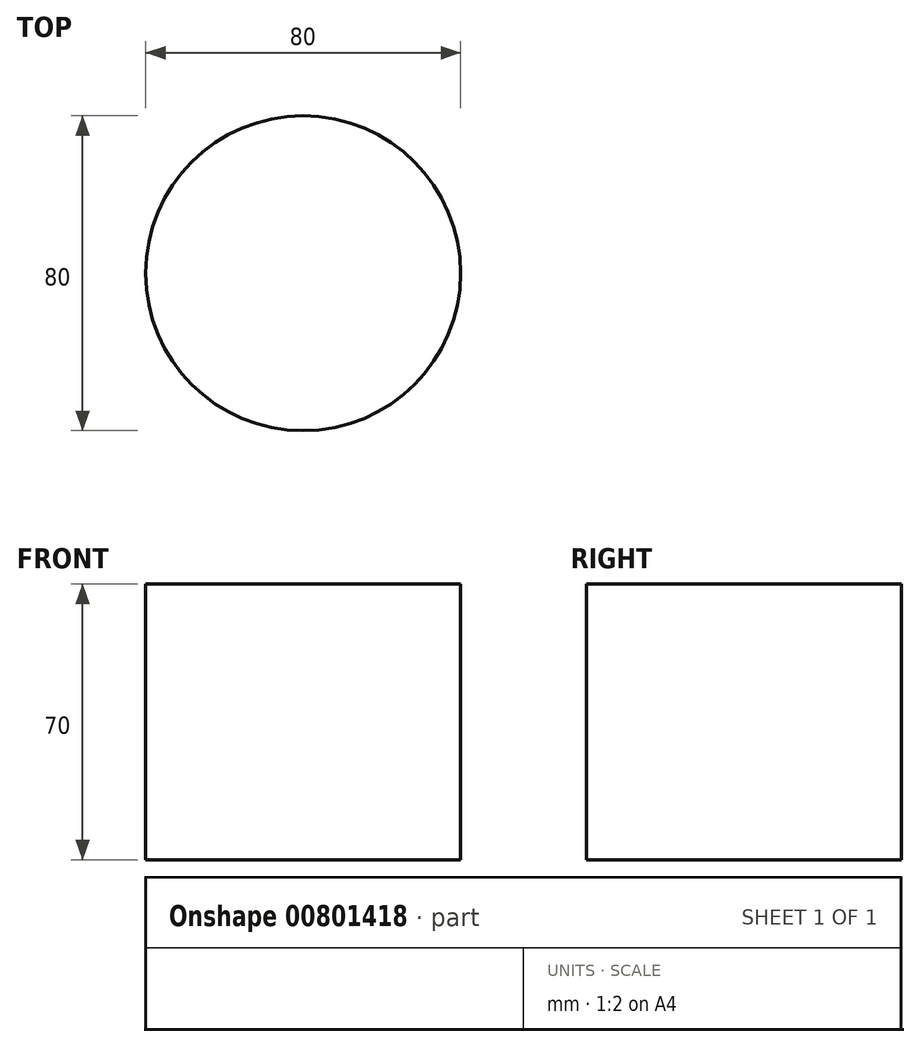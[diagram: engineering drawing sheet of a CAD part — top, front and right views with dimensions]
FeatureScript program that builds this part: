
annotation { "Feature Type Name" : "Feature", "Feature Type Description" : "" }
export const myFeature = defineFeature(function(context is Context, id is Id, definition is map)
    precondition{}
    {
        {
            var Q0;
            Q0=qCreatedBy(makeId("Top.planeOp"),FACE);
            var sketch = newSketch(context, id + "F0", { "sketchPlane" : qUnion([Q0])});
            skCircle(sketch, "E0", {"center": v(0, 0) * mm, "radius": 40 * mm});
            skSolve(sketch);
        }
        {
            var Q0;
            Q0=makeQuery(id+"F0.imprint","IMPRINT",FACE,{"disambiguationData":[TD([[makeQuery(id+"F0.imprint","IMPRINT",EDGE,{"derivedFrom":sQuery(id+"F0.wireOp",EDGE,"E0")}),1.0]])]});
            extrude(context, id + "F1", {"entities" : qUnion([Q0]), "depth" : 70 * mm, "offsetDistance" : 25 * mm});
        }
    });
